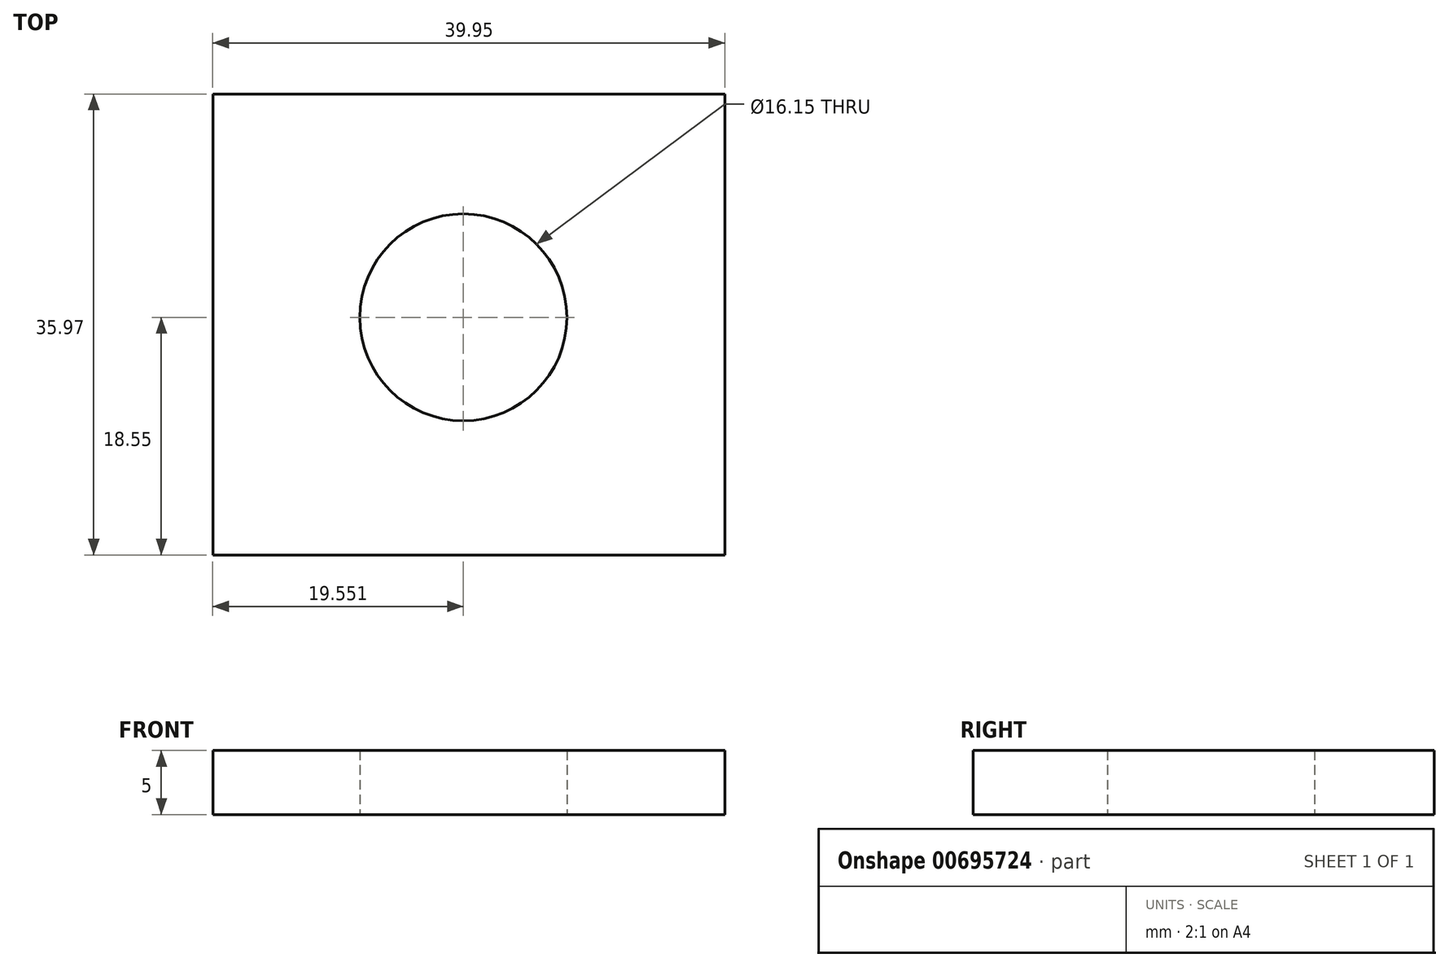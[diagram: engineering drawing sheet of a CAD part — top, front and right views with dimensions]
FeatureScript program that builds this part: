
annotation { "Feature Type Name" : "Feature", "Feature Type Description" : "" }
export const myFeature = defineFeature(function(context is Context, id is Id, definition is map)
    precondition{}
    {
        {
            var Q0;
            Q0=qCreatedBy(makeId("Top.planeOp"),FACE);
            var sketch = newSketch(context, id + "F0", { "sketchPlane" : qUnion([Q0])});
            skLineSegment(sketch, "E0.bottom", {"start": v(-15.16, 17.42) * mm, "end": v(24.79, 17.42) * mm});
            skLineSegment(sketch, "E0.top", {"start": v(-15.16, -18.55) * mm, "end": v(24.79, -18.55) * mm});
            skLineSegment(sketch, "E0.left", {"start": v(-15.16, 17.42) * mm, "end": v(-15.16, -18.55) * mm});
            skLineSegment(sketch, "E0.right", {"start": v(24.79, 17.42) * mm, "end": v(24.79, -18.55) * mm});
            skCircle(sketch, "E1", {"center": v(4.4, 0) * mm, "radius": 8.07 * mm});
            skSolve(sketch);
        }
        {
            var Q0;
            Q0=makeQuery(id+"F0.imprint","IMPRINT",FACE,{"disambiguationData":[TD([[makeQuery(id+"F0.imprint","IMPRINT",EDGE,{"derivedFrom":sQuery(id+"F0.wireOp",EDGE,"E0.bottom")}),-1.0]])]});
            extrude(context, id + "F1", {"entities" : qUnion([Q0]), "depth" : 5 * mm, "offsetDistance" : 25 * mm});
        }
    });
